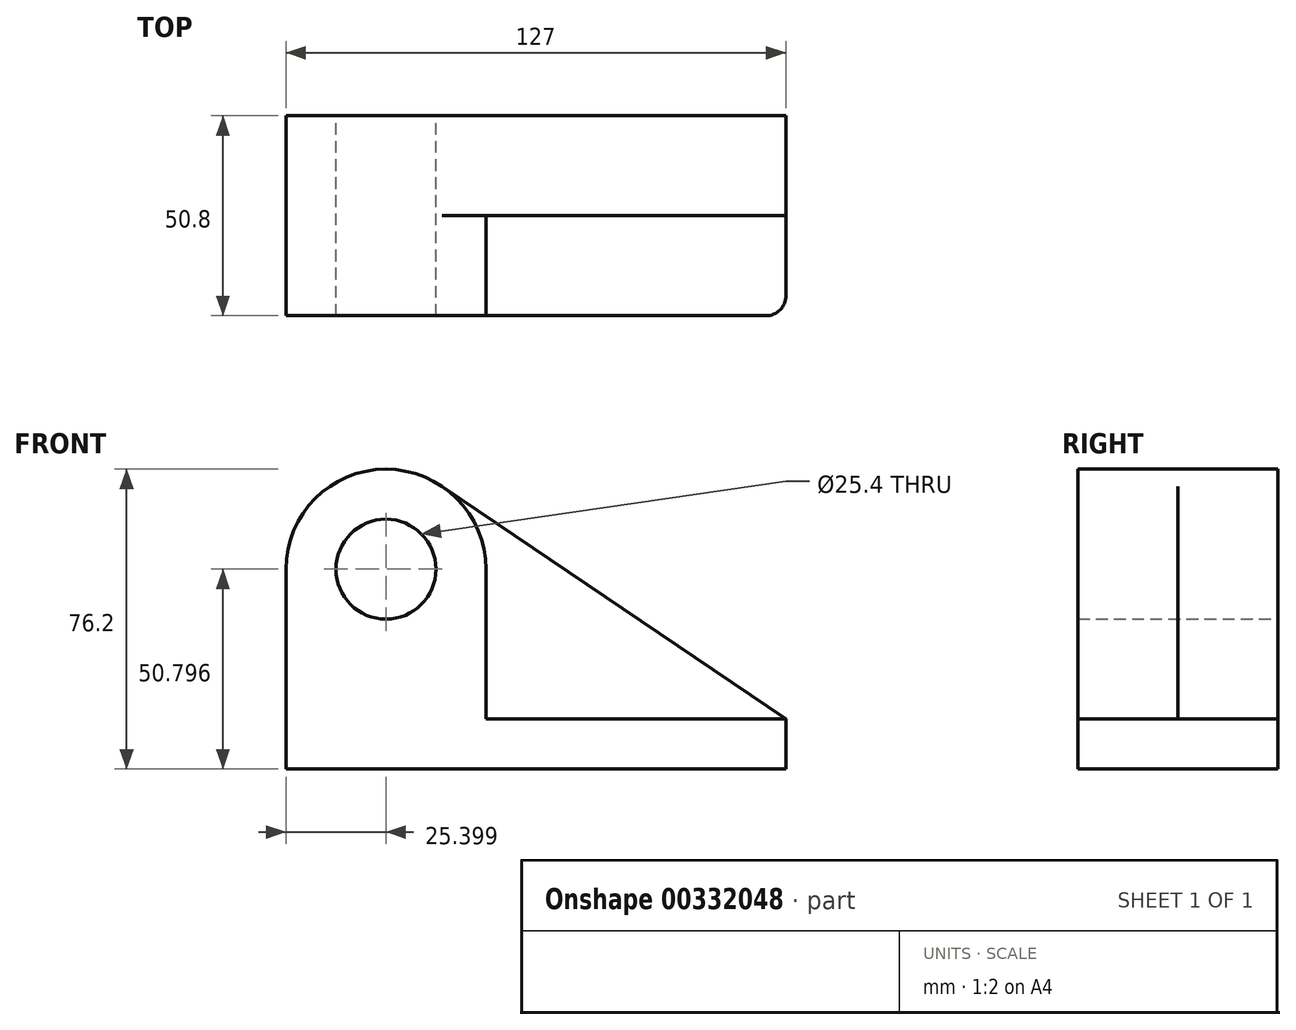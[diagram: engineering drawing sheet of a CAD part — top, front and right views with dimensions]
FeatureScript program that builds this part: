
annotation { "Feature Type Name" : "Feature", "Feature Type Description" : "" }
export const myFeature = defineFeature(function(context is Context, id is Id, definition is map)
    precondition{}
    {
        {
            var Q0;
            Q0=qCreatedBy(makeId("Front.planeOp"),FACE);
            var sketch = newSketch(context, id + "F0", { "sketchPlane" : qUnion([Q0])});
            skCircle(sketch, "E0", {"center": v(-44.5, 17.18) * mm, "radius": 12.7 * mm});
            skArc(sketch, "E1", {"start": v(-30.26, 38.21) * mm, "mid": v(-56.4, 39.61) * mm, "end": v(-69.9, 17.18) * mm});
            skLineSegment(sketch, "E2", {"start": v(-69.9, 17.18) * mm, "end": v(-69.9, -33.62) * mm});
            skLineSegment(sketch, "E3", {"start": v(-69.9, -33.62) * mm, "end": v(57.1, -33.62) * mm});
            skLineSegment(sketch, "E4", {"start": v(57.1, -33.62) * mm, "end": v(57.1, -20.92) * mm});
            skLineSegment(sketch, "E5", {"start": v(57.1, -20.92) * mm, "end": v(-30.26, 38.21) * mm});
            skSolve(sketch);
        }
        {
            var Q0;
            Q0=makeQuery(id+"F0.imprint","IMPRINT",FACE,{"disambiguationData":[TD([[makeQuery(id+"F0.imprint","IMPRINT",EDGE,{"derivedFrom":sQuery(id+"F0.wireOp",EDGE,"E0")}),-1.0]])]});
            extrude(context, id + "F1", {"entities" : qUnion([Q0]), "depth" : 25.4 * mm});
        }
        {
            var Q0;
            Q0=makeQuery(id+"F1.opExtrude","CAP_FACE",FACE,{"disambiguationData":[OSD([sQuery(id+"F0.wireOp",EDGE,"E0"),sQuery(id+"F0.wireOp",EDGE,"E1"),sQuery(id+"F0.wireOp",EDGE,"E2"),sQuery(id+"F0.wireOp",EDGE,"E3"),sQuery(id+"F0.wireOp",EDGE,"E4"),sQuery(id+"F0.wireOp",EDGE,"E5")])],"isStart":false});
            var sketch = newSketch(context, id + "F2", { "sketchPlane" : qUnion([Q0])});
            skArc(sketch, "E6", {"start": v(-19.1, 17.18) * mm, "mid": v(-44.5, 42.58) * mm, "end": v(-69.9, 17.18) * mm});
            skCircle(sketch, "E7", {"center": v(-44.5, 17.18) * mm, "radius": 12.7 * mm});
            skLineSegment(sketch, "E8.bottom", {"start": v(57.1, -20.92) * mm, "end": v(-19.1, -20.92) * mm});
            skLineSegment(sketch, "E8.top", {"start": v(57.1, -33.62) * mm, "end": v(-69.9, -33.62) * mm});
            skLineSegment(sketch, "E8.left", {"start": v(57.1, -20.92) * mm, "end": v(57.1, -33.62) * mm});
            skLineSegment(sketch, "E8.right", {"start": v(-69.9, -20.92) * mm, "end": v(-69.9, -33.62) * mm});
            skLineSegment(sketch, "E9", {"start": v(-44.5, 17.18) * mm, "end": v(-69.9, 17.18) * mm});
            skLineSegment(sketch, "E10", {"start": v(-69.9, 17.18) * mm, "end": v(-69.9, -20.92) * mm});
            skLineSegment(sketch, "E11", {"start": v(-44.5, 17.18) * mm, "end": v(-19.1, 17.18) * mm});
            skLineSegment(sketch, "E12", {"start": v(-19.1, 17.18) * mm, "end": v(-19.1, -20.92) * mm});
            skSolve(sketch);
        }
        {
            var Q0;
            Q0=makeQuery(id+"F2.imprint","IMPRINT",FACE,{"disambiguationData":[TD([[makeQuery(id+"F2.imprint","IMPRINT",EDGE,{"derivedFrom":sQuery(id+"F2.wireOp",EDGE,"E8.bottom")}),1.0]])]});
            var Q1;
            {var subQ0=sQuery(id+"F2.wireOp",EDGE,"E9");var subQ3=sQuery(id+"F2.wireOp",EDGE,"E7");var subQ4=makeQuery(id+"F2.imprint","INTERSECT",VERTEX,{"derivedFrom":[subQ3,subQ0]});Q1=makeQuery(id+"F2.imprint","IMPRINT",FACE,{"disambiguationData":[TD([[makeQuery(id+"F2.imprint","IMPRINT",EDGE,{"disambiguationData":[TD([[subQ4,1.0]])],"derivedFrom":subQ3}),-1.0]])]});}
            extrude(context, id + "F3", {"entities" : qUnion([Q0, Q1]), "operationType" : NewBodyOperationType.ADD, "depth" : 25.4 * mm});
        }
        {
            var Q0;
            Q0=makeQuery(id+"F3.opExtrude","CAP_EDGE",EDGE,{"disambiguationData":[OSD([sQuery(id+"F2.wireOp",EDGE,"E8.left")])],"isStart":false});
            fillet(context, id + "F4", {"entities" : qUnion([Q0]), "radius" : 5.08 * mm, "tangentPropagation" : true, "allowEdgeOverflow" : false});
        }
    });
